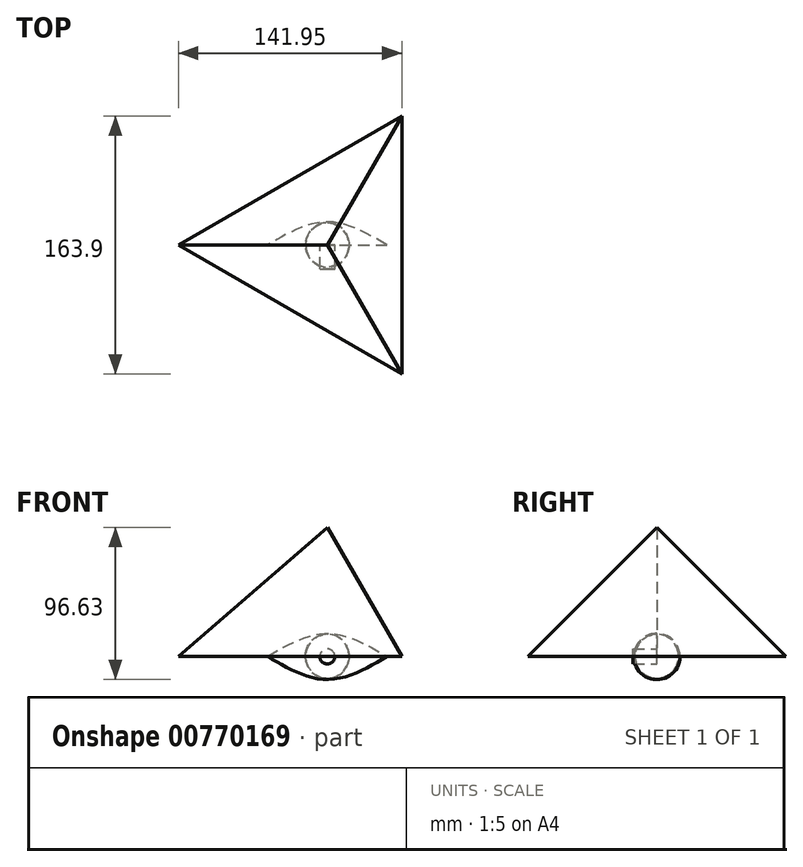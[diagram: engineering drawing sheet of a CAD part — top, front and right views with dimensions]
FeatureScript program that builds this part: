
annotation { "Feature Type Name" : "Feature", "Feature Type Description" : "" }
export const myFeature = defineFeature(function(context is Context, id is Id, definition is map)
    precondition{}
    {
        {
            var Q0;
            Q0=qCreatedBy(makeId("Front.planeOp"),FACE);
            var sketch = newSketch(context, id + "F0", { "sketchPlane" : qUnion([Q0])});
            skLineSegment(sketch, "E0", {"start": v(-38.12, 0) * mm, "end": v(37.86, 0) * mm});
            skFitSpline(sketch, "E1", {"points": [v(-38.12, 0) * mm, v(0, 14.68) * mm, v(37.86, 0) * mm], "startDerivative": vector(76.2, 44.02) * mm, "endDerivative": vector(75.76, -44.06) * mm});
            skSolve(sketch);
        }
        {
            var Q0;
            Q0=makeQuery(id+"F0.imprint","IMPRINT",FACE,{"disambiguationData":[TD([[makeQuery(id+"F0.imprint","IMPRINT",EDGE,{"derivedFrom":sQuery(id+"F0.wireOp",EDGE,"E0")}),1.0]])]});
            var Q1;
            Q1=sQuery(id+"F0.wireOp",EDGE,"E0");
            revolve(context, id + "F1", {"surfaceOperationType" : NewSurfaceOperationType.NEW, "entities" : qUnion([Q0]), "axis" : qUnion([Q1]), "revolveType" : RevolveType.FULL});
        }
        {
            var Q0;
            Q0=qCreatedBy(makeId("Front.planeOp"),FACE);
            var sketch = newSketch(context, id + "F2", { "sketchPlane" : qUnion([Q0])});
            skLineSegment(sketch, "E2", {"start": v(0, 14.06) * mm, "end": v(0, -13.84) * mm});
            skArc(sketch, "E3", {"start": v(0, 14.06) * mm, "mid": v(-14.06, 0.11) * mm, "end": v(0, -13.84) * mm});
            skSolve(sketch);
        }
        {
            var Q0;
            Q0 = qSketchRegion(id + "F2", true);
            var Q1;
            Q1=sQuery(id+"F2.wireOp",EDGE,"E3");
            var Q2;
            Q2=sQuery(id+"F2.wireOp",EDGE,"E2");
            revolve(context, id + "F3", {"surfaceOperationType" : NewSurfaceOperationType.NEW, "entities" : qUnion([Q0]), "surfaceEntities" : qUnion([Q1]), "axis" : qUnion([Q2]), "revolveType" : RevolveType.FULL});
        }
        {
            var Q0;
            Q0=qCreatedBy(makeId("Front.planeOp"),FACE);
            var sketch = newSketch(context, id + "F4", { "sketchPlane" : qUnion([Q0])});
            skCircle(sketch, "E4", {"center": v(0, 0) * mm, "radius": 4.79 * mm});
            skSolve(sketch);
        }
        {
            var Q0;
            Q0 = qSketchRegion(id + "F4", true);
            extrude(context, id + "F5", {"entities" : qUnion([Q0]), "depth" : 15.24 * mm, "offsetDistance" : 25.4 * mm});
        }
        {
            var Q0;
            Q0=qCreatedBy(makeId("Top.planeOp"),FACE);
            var sketch = newSketch(context, id + "F6", { "sketchPlane" : qUnion([Q0])});
            skCircle(sketch, "E5.cCircle", {"center": v(0, 0) * mm, "radius": 47.32 * mm, "construction": true});
            skLineSegment(sketch, "E5.0", {"start": v(47.32, 81.95) * mm, "end": v(47.32, -81.95) * mm});
            skLineSegment(sketch, "E5.1", {"start": v(47.32, -81.95) * mm, "end": v(-94.63, 0) * mm});
            skLineSegment(sketch, "E5.2", {"start": v(-94.63, 0) * mm, "end": v(47.32, 81.95) * mm});
            skPoint(sketch, "E5.0.midPoint", {"position": v(47.32, 0) * mm});
            skSolve(sketch);
        }
        {
            var Q0;
            Q0=makeQuery(id+"F6.imprint","IMPRINT",FACE,{"disambiguationData":[TD([[makeQuery(id+"F6.imprint","IMPRINT",EDGE,{"derivedFrom":sQuery(id+"F6.wireOp",EDGE,"E5.0")}),-1.0]])]});
            extrude(context, id + "F7", {"entities" : qUnion([Q0]), "depth" : 127.56 * mm, "offsetDistance" : 25.4 * mm, "hasDraft" : true, "draftAngle" : 30 * degree, "draftPullDirection" : true});
        }
    });
